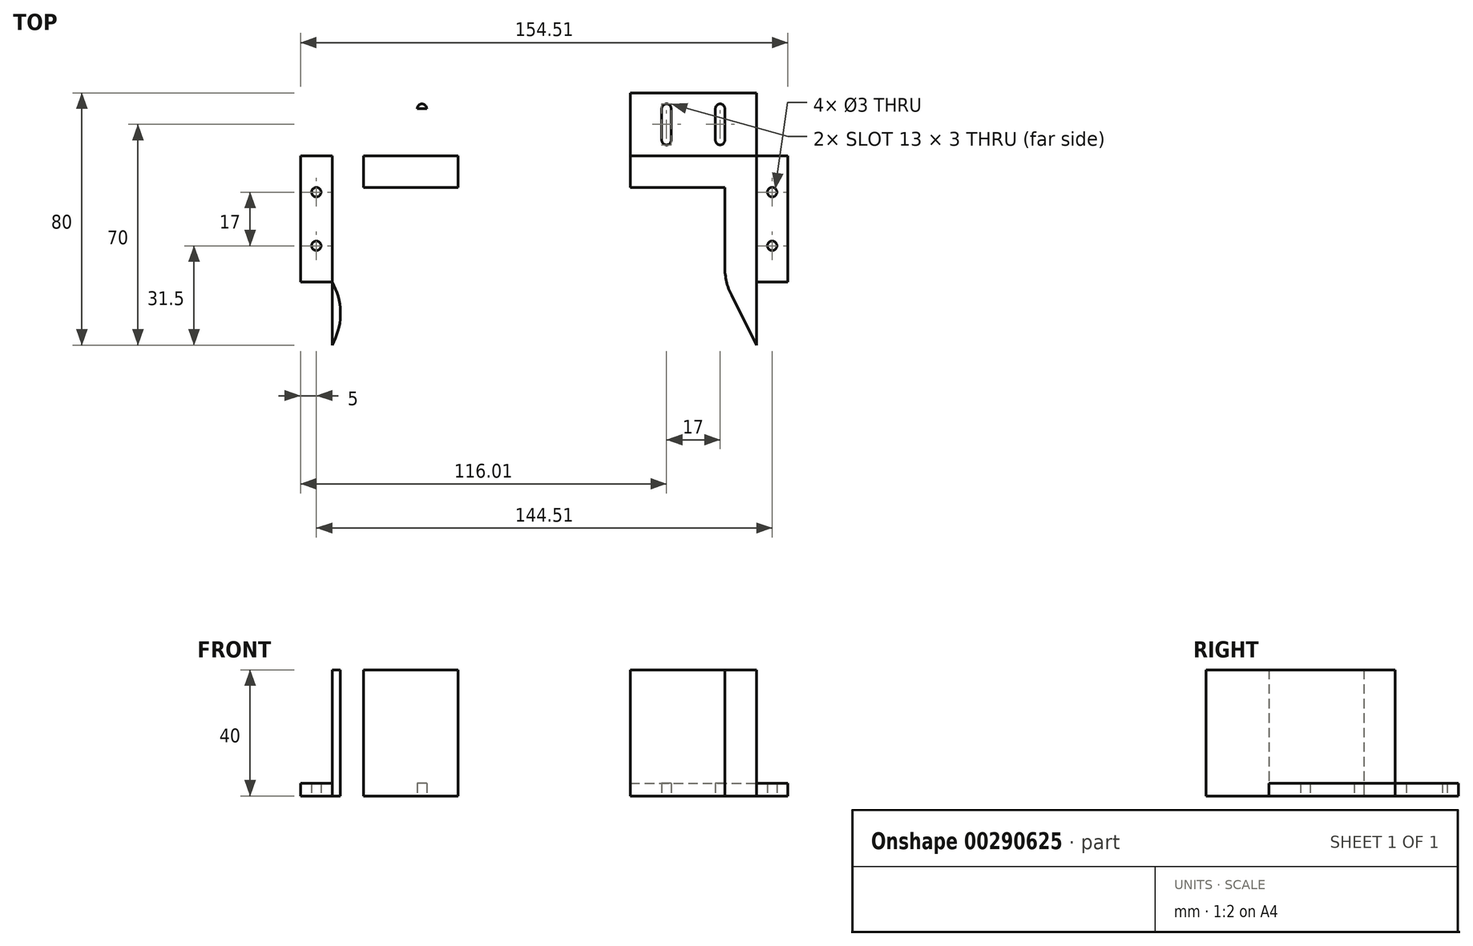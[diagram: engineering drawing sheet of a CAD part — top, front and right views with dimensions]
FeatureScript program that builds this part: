
annotation { "Feature Type Name" : "Feature", "Feature Type Description" : "" }
export const myFeature = defineFeature(function(context is Context, id is Id, definition is map)
    precondition{}
    {
        {
            var Q0;
            Q0=qCreatedBy(makeId("Top.planeOp"),FACE);
            var sketch = newSketch(context, id + "F0", { "sketchPlane" : qUnion([Q0])});
            skLineSegment(sketch, "E0.bottom", {"start": v(-30, 10) * mm, "end": v(0, 10) * mm});
            skLineSegment(sketch, "E0.top", {"start": v(-30, 0) * mm, "end": v(0, 0) * mm});
            skLineSegment(sketch, "E0.left", {"start": v(-30, 10) * mm, "end": v(-30, 0) * mm});
            skLineSegment(sketch, "E0.right", {"start": v(0, 10) * mm, "end": v(0, 0) * mm});
            skLineSegment(sketch, "E1.bottom", {"start": v(0, 10) * mm, "end": v(10, 10) * mm});
            skLineSegment(sketch, "E1.top", {"start": v(0, -30) * mm, "end": v(10, -30) * mm});
            skLineSegment(sketch, "E1.left", {"start": v(0, 10) * mm, "end": v(0, -30) * mm});
            skLineSegment(sketch, "E1.right", {"start": v(10, 10) * mm, "end": v(10, -30) * mm});
            skLineSegment(sketch, "E2.bottom", {"start": v(-30, 10) * mm, "end": v(10, 10) * mm});
            skLineSegment(sketch, "E2.top", {"start": v(-30, 30) * mm, "end": v(10, 30) * mm});
            skLineSegment(sketch, "E2.left", {"start": v(-30, 10) * mm, "end": v(-30, 30) * mm});
            skLineSegment(sketch, "E2.right", {"start": v(10, 10) * mm, "end": v(10, 30) * mm});
            skLineSegment(sketch, "E3.top", {"start": v(10, -30) * mm, "end": v(20, -30) * mm});
            skLineSegment(sketch, "E3.left", {"start": v(10, 30) * mm, "end": v(10, -30) * mm});
            skLineSegment(sketch, "E3.right", {"start": v(20, 10) * mm, "end": v(20, -30) * mm});
            skLineSegment(sketch, "E4", {"start": v(10, -30) * mm, "end": v(10, -50) * mm});
            skLineSegment(sketch, "E5", {"start": v(10, -50) * mm, "end": v(0, -30) * mm});
            skLineSegment(sketch, "E6", {"start": v(10, 10) * mm, "end": v(20, 10) * mm});
            skLineSegment(sketch, "E7.bottom", {"start": v(-20, 25) * mm, "end": v(-17, 25) * mm});
            skLineSegment(sketch, "E7.top", {"start": v(-20, 15) * mm, "end": v(-17, 15) * mm});
            skLineSegment(sketch, "E7.left", {"start": v(-20, 25) * mm, "end": v(-20, 15) * mm});
            skLineSegment(sketch, "E7.right", {"start": v(-17, 25) * mm, "end": v(-17, 15) * mm});
            skLineSegment(sketch, "E8.bottom", {"start": v(-3, 25) * mm, "end": v(0, 25) * mm});
            skLineSegment(sketch, "E8.top", {"start": v(-3, 15) * mm, "end": v(0, 15) * mm});
            skLineSegment(sketch, "E8.left", {"start": v(-3, 25) * mm, "end": v(-3, 15) * mm});
            skLineSegment(sketch, "E8.right", {"start": v(0, 25) * mm, "end": v(0, 15) * mm});
            skArc(sketch, "E9", {"start": v(-17, 25) * mm, "mid": v(-18.5, 26.5) * mm, "end": v(-20, 25) * mm});
            skArc(sketch, "E10", {"start": v(-20, 15) * mm, "mid": v(-18.5, 13.5) * mm, "end": v(-17, 15) * mm});
            skArc(sketch, "E11", {"start": v(0, 25) * mm, "mid": v(-1.5, 26.5) * mm, "end": v(-3, 25) * mm});
            skArc(sketch, "E12", {"start": v(-3, 15) * mm, "mid": v(-1.5, 13.5) * mm, "end": v(0, 15) * mm});
            skLineSegment(sketch, "E13", {"start": v(15, 10) * mm, "end": v(15, -30) * mm, "construction": true});
            skCircle(sketch, "E14", {"center": v(15, -1.5) * mm, "radius": 1.5 * mm});
            skCircle(sketch, "E15", {"center": v(15, -18.5) * mm, "radius": 1.5 * mm});
            skLineSegment(sketch, "E16", {"start": v(-57.25, 30.68) * mm, "end": v(-57.25, -16.41) * mm, "construction": true});
            skArc(sketch, "E17.MirrorCS", {"start": v(-97.5, 25) * mm, "mid": v(-96, 26.5) * mm, "end": v(-94.5, 25) * mm});
            skLineSegment(sketch, "E18.MirrorCS", {"start": v(-94.5, 25) * mm, "end": v(-97.5, 25) * mm});
            skArc(sketch, "E19.MirrorCS", {"start": v(-94.5, 15) * mm, "mid": v(-96, 13.5) * mm, "end": v(-97.5, 15) * mm});
            skArc(sketch, "E20.MirrorCS", {"start": v(-111.5, 15) * mm, "mid": v(-113, 13.5) * mm, "end": v(-114.5, 15) * mm});
            skLineSegment(sketch, "E21.MirrorCS", {"start": v(-111.5, 25) * mm, "end": v(-114.5, 25) * mm});
            skArc(sketch, "E22.MirrorCS", {"start": v(-114.5, 25) * mm, "mid": v(-113, 26.5) * mm, "end": v(-111.5, 25) * mm});
            skLineSegment(sketch, "E23.MirrorCS", {"start": v(-111.5, 15) * mm, "end": v(-114.5, 15) * mm});
            skLineSegment(sketch, "E24.MirrorCS", {"start": v(-94.5, 15) * mm, "end": v(-97.5, 15) * mm});
            skLineSegment(sketch, "E25.MirrorCS", {"start": v(-124.5, 30) * mm, "end": v(-124.5, -30) * mm});
            skLineSegment(sketch, "E26.MirrorCS", {"start": v(-124.5, -30) * mm, "end": v(-134.5, -30) * mm});
            skLineSegment(sketch, "E27.MirrorCS", {"start": v(-84.5, 10) * mm, "end": v(-114.5, 10) * mm});
            skLineSegment(sketch, "E28.MirrorCS", {"start": v(-114.5, 10) * mm, "end": v(-114.5, 0) * mm});
            skLineSegment(sketch, "E29.MirrorCS", {"start": v(-114.5, 10) * mm, "end": v(-124.5, 10) * mm});
            skCircle(sketch, "E30.MirrorC", {"center": v(-129.5, -1.5) * mm, "radius": 1.5 * mm});
            skLineSegment(sketch, "E31.MirrorCS", {"start": v(-124.5, 10) * mm, "end": v(-134.5, 10) * mm});
            skCircle(sketch, "E32.MirrorC", {"center": v(-129.5, -18.5) * mm, "radius": 1.5 * mm});
            skLineSegment(sketch, "E33.MirrorCS", {"start": v(-114.5, 10) * mm, "end": v(-114.5, -30) * mm});
            skLineSegment(sketch, "E34.MirrorCS", {"start": v(-84.5, 10) * mm, "end": v(-124.5, 10) * mm});
            skLineSegment(sketch, "E35.MirrorCS", {"start": v(-124.5, 10) * mm, "end": v(-124.5, -30) * mm});
            skLineSegment(sketch, "E36.MirrorCS", {"start": v(-134.5, 10) * mm, "end": v(-134.5, -30) * mm});
            skLineSegment(sketch, "E37.MirrorCS", {"start": v(-84.5, 30) * mm, "end": v(-124.5, 30) * mm});
            skLineSegment(sketch, "E38.MirrorCS", {"start": v(-84.5, 10) * mm, "end": v(-84.5, 30) * mm});
            skLineSegment(sketch, "E39.MirrorCS", {"start": v(-124.5, 10) * mm, "end": v(-124.5, 30) * mm});
            skLineSegment(sketch, "E40.MirrorCS", {"start": v(-97.5, 25) * mm, "end": v(-97.5, 15) * mm});
            skLineSegment(sketch, "E41.MirrorCS", {"start": v(-114.5, -30) * mm, "end": v(-124.5, -30) * mm});
            skLineSegment(sketch, "E42.MirrorCS", {"start": v(-84.5, 10) * mm, "end": v(-84.5, 0) * mm});
            skLineSegment(sketch, "E43.MirrorCS", {"start": v(-84.5, 0) * mm, "end": v(-114.5, 0) * mm});
            skLineSegment(sketch, "E44.MirrorCS", {"start": v(-124.5, -30) * mm, "end": v(-124.5, -50) * mm});
            skLineSegment(sketch, "E45.MirrorCS", {"start": v(-129.5, 10) * mm, "end": v(-129.5, -30) * mm, "construction": true});
            skLineSegment(sketch, "E46.MirrorCS", {"start": v(-114.5, 25) * mm, "end": v(-114.5, 15) * mm});
            skLineSegment(sketch, "E47.MirrorCS", {"start": v(-124.5, -50) * mm, "end": v(-114.5, -30) * mm});
            skLineSegment(sketch, "E48.MirrorCS", {"start": v(-94.5, 25) * mm, "end": v(-94.5, 15) * mm});
            skLineSegment(sketch, "E49.MirrorCS", {"start": v(-111.5, 25) * mm, "end": v(-111.5, 15) * mm});
            skSolve(sketch);
        }
        {
            var Q0;
            {var subQ3=sQuery(id+"F0.wireOp",EDGE,"E2.top");Q0=makeQuery(id+"F0.imprint","IMPRINT",FACE,{"disambiguationData":[TD([[makeQuery(id+"F0.imprint","IMPRINT",EDGE,{"derivedFrom":subQ3}),-1.0]])]});}
            var Q1;
            {var subQ2=sQuery(id+"F0.wireOp",EDGE,"E3.top");Q1=makeQuery(id+"F0.imprint","IMPRINT",FACE,{"disambiguationData":[TD([[makeQuery(id+"F0.imprint","IMPRINT",EDGE,{"derivedFrom":subQ2}),1.0]])]});}
            var Q2;
            Q2=makeQuery(id+"F0.imprint","IMPRINT",FACE,{"disambiguationData":[TD([[makeQuery(id+"F0.imprint","IMPRINT",EDGE,{"derivedFrom":sQuery(id+"F0.wireOp",EDGE,"E17.MirrorCS")}),1.0]])]});
            var Q3;
            Q3=makeQuery(id+"F0.imprint","IMPRINT",FACE,{"disambiguationData":[TD([[makeQuery(id+"F0.imprint","IMPRINT",EDGE,{"derivedFrom":sQuery(id+"F0.wireOp",EDGE,"E26.MirrorCS")}),-1.0]])]});
            extrude(context, id + "F1", {"entities" : qUnion([Q0, Q1, Q2, Q3]), "depth" : 4 * mm});
        }
        {
            var Q0;
            {var subQ0=sQuery(id+"F0.wireOp",EDGE,"E0.top");Q0=makeQuery(id+"F0.imprint","IMPRINT",FACE,{"disambiguationData":[TD([[makeQuery(id+"F0.imprint","IMPRINT",EDGE,{"derivedFrom":subQ0}),1.0]])]});}
            var Q1;
            {var subQ6=sQuery(id+"F0.wireOp",EDGE,"E1.top");Q1=makeQuery(id+"F0.imprint","IMPRINT",FACE,{"disambiguationData":[TD([[makeQuery(id+"F0.imprint","IMPRINT",EDGE,{"derivedFrom":subQ6}),1.0]])]});}
            var Q2;
            Q2=makeQuery(id+"F0.imprint","IMPRINT",FACE,{"disambiguationData":[TD([[makeQuery(id+"F0.imprint","IMPRINT",EDGE,{"derivedFrom":sQuery(id+"F0.wireOp",EDGE,"E0.left")}),-1.0]])]});
            var Q3;
            Q3=makeQuery(id+"F0.imprint","IMPRINT",FACE,{"disambiguationData":[TD([[makeQuery(id+"F0.imprint","IMPRINT",EDGE,{"derivedFrom":sQuery(id+"F0.wireOp",EDGE,"E1.top")}),-1.0]])]});
            var Q4;
            {var subQ4=sQuery(id+"F0.wireOp",EDGE,"E42.MirrorCS");Q4=makeQuery(id+"F0.imprint","IMPRINT",FACE,{"disambiguationData":[TD([[makeQuery(id+"F0.imprint","IMPRINT",EDGE,{"derivedFrom":subQ4}),-1.0]])]});}
            var Q5;
            Q5=makeQuery(id+"F0.imprint","IMPRINT",FACE,{"disambiguationData":[TD([[makeQuery(id+"F0.imprint","IMPRINT",EDGE,{"derivedFrom":sQuery(id+"F0.wireOp",EDGE,"E190.MirrorCS")}),-1.0]])]});
            var Q6;
            {var subQ0=sQuery(id+"F0.wireOp",EDGE,"E35.MirrorCS");Q6=makeQuery(id+"F0.imprint","IMPRINT",FACE,{"disambiguationData":[TD([[makeQuery(id+"F0.imprint","IMPRINT",EDGE,{"derivedFrom":subQ0}),1.0]])]});}
            var Q7;
            Q7=makeQuery(id+"F0.imprint","IMPRINT",FACE,{"disambiguationData":[TD([[makeQuery(id+"F0.imprint","IMPRINT",EDGE,{"derivedFrom":sQuery(id+"F0.wireOp",EDGE,"E41.MirrorCS")}),1.0]])]});
            extrude(context, id + "F2", {"entities" : qUnion([Q0, Q1, Q2, Q3, Q4, Q5, Q6, Q7]), "operationType" : NewBodyOperationType.ADD, "depth" : 40 * mm});
        }
        {
            var Q0;
            Q0=makeQuery(id+"F2.opExtrude","SWEPT_EDGE",EDGE,{"disambiguationData":[OSD([sQuery(id+"F0.wireOp",EDGE,"E1.top"),sQuery(id+"F0.wireOp",EDGE,"E1.left"),sQuery(id+"F0.wireOp",EDGE,"E5")])]});
            var Q1;
            Q1=makeQuery(id+"F2.opExtrude","SWEPT_EDGE",EDGE,{"disambiguationData":[OSD([sQuery(id+"F0.wireOp",EDGE,"E33.MirrorCS"),sQuery(id+"F0.wireOp",EDGE,"E41.MirrorCS"),sQuery(id+"F0.wireOp",EDGE,"E47.MirrorCS")])]});
            fillet(context, id + "F3", {"entities" : qUnion([Q0, Q1]), "radius" : 20 * mm, "tangentPropagation" : true, "allowEdgeOverflow" : false});
        }
    });
